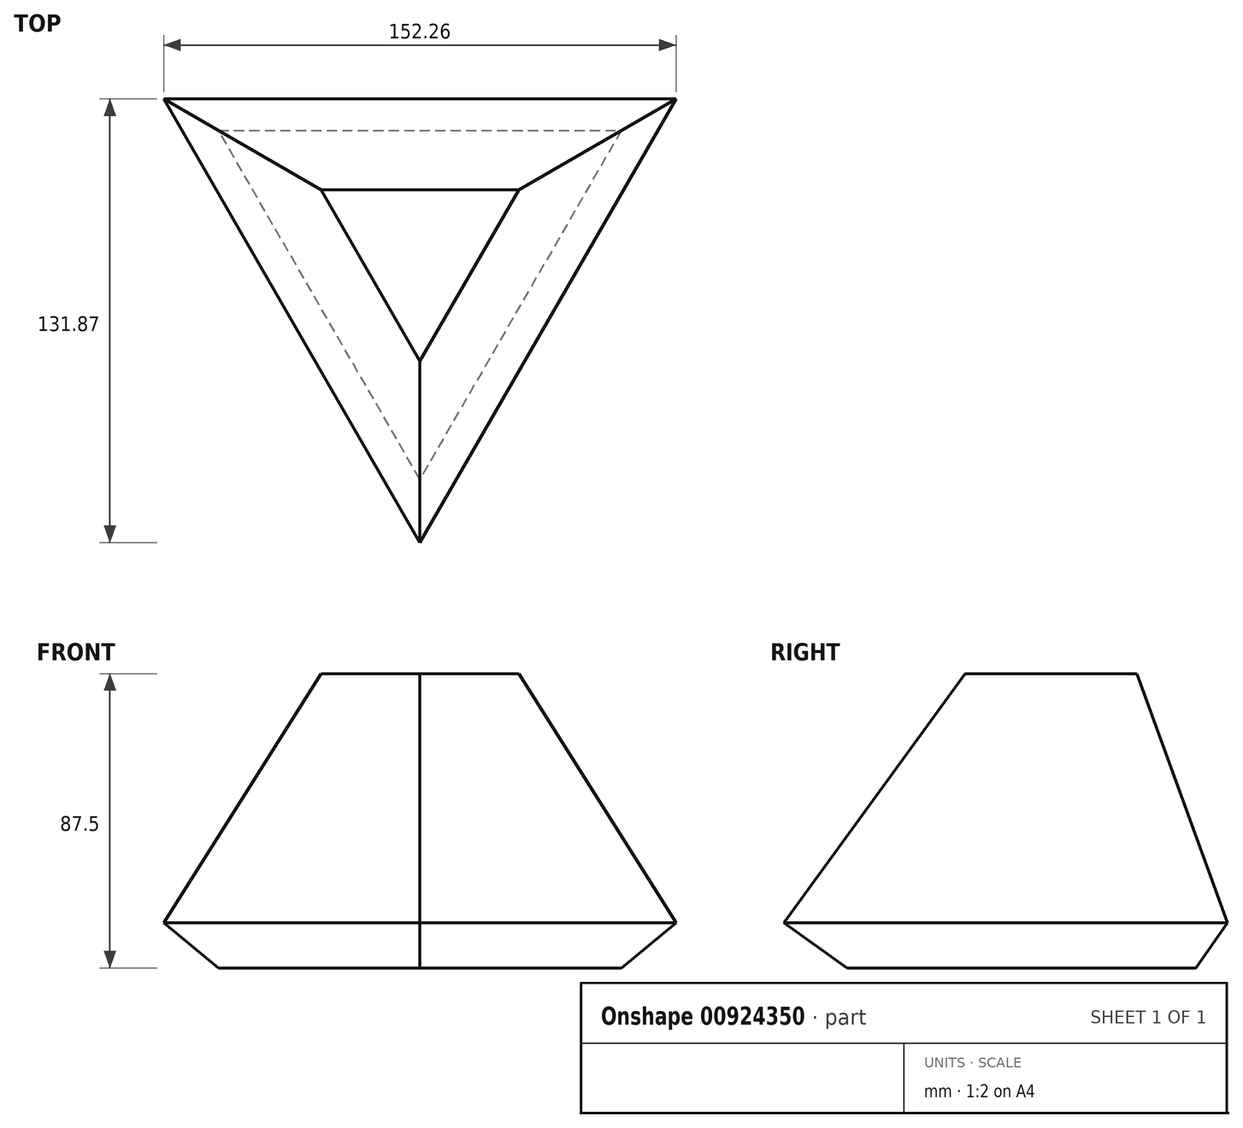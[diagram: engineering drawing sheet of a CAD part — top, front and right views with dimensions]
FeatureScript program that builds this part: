
annotation { "Feature Type Name" : "Feature", "Feature Type Description" : "" }
export const myFeature = defineFeature(function(context is Context, id is Id, definition is map)
    precondition{}
    {
        {
            var Q0;
            Q0=qCreatedBy(makeId("Top.planeOp"),FACE);
            var sketch = newSketch(context, id + "F0", { "sketchPlane" : qUnion([Q0])});
            skCircle(sketch, "E0.cCircle", {"center": v(0, 0) * mm, "radius": 48.84 * mm, "construction": true});
            skLineSegment(sketch, "E0.0", {"start": v(-84.6, 48.84) * mm, "end": v(84.6, 48.84) * mm});
            skLineSegment(sketch, "E0.1", {"start": v(84.6, 48.84) * mm, "end": v(0, -97.68) * mm});
            skLineSegment(sketch, "E0.2", {"start": v(0, -97.68) * mm, "end": v(-84.6, 48.84) * mm});
            skPoint(sketch, "E0.0.midPoint", {"position": v(0, 48.84) * mm});
            skSolve(sketch);
        }
        {
            var Q0;
            Q0=makeQuery(id+"F0.imprint","IMPRINT",FACE,{"disambiguationData":[TD([[makeQuery(id+"F0.imprint","IMPRINT",EDGE,{"derivedFrom":sQuery(id+"F0.wireOp",EDGE,"E0.0")}),-1.0]])]});
            extrude(context, id + "F1", {"entities" : qUnion([Q0]), "depth" : 87.5 * mm, "offsetDistance" : 25 * mm, "hasDraft" : true, "draftAngle" : 20 * degree, "draftPullDirection" : true});
        }
        {
            var Q0;
            Q0=makeQuery(id+"F1.opExtrude","CAP_EDGE",EDGE,{"disambiguationData":[OSD([sQuery(id+"F0.wireOp",EDGE,"E0.1")])],"isStart":true});
            var Q1;
            Q1=makeQuery(id+"F1.opExtrude","CAP_EDGE",EDGE,{"disambiguationData":[OSD([sQuery(id+"F0.wireOp",EDGE,"E0.2")])],"isStart":true});
            var Q2;
            Q2=makeQuery(id+"F1.opExtrude","CAP_EDGE",EDGE,{"disambiguationData":[OSD([sQuery(id+"F0.wireOp",EDGE,"E0.0")])],"isStart":true});
            chamfer(context, id + "F2", {"entities" : qUnion([Q0, Q1, Q2]), "width" : 10 * mm, "tangentPropagation" : true});
        }
    });
